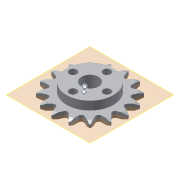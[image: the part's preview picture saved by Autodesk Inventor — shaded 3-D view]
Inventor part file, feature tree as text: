
AUTODESK INVENTOR PART (.ipt)
format: ipt  version: 2013 (Build 170138000, 138)  size: 414,208 bytes
history: native  units: in
note: dims shown in document units (in); Inventor stores cm internally (conversion verified against a paired STEP export)
features: other x17, plane x1
ambient origin geometry x8: Origin, YZ Plane, XZ Plane, XY Plane, X Axis, Y Axis, Z Axis, Center Point
bodies: Solid1 (feature_tree)
feature tree (18):
  other  "Tetrix sprocket 16T.ipt"
  other  "sprocket_25_16t_tetrix::Tetrix sprocket 16T.ipt"
  other  "TaggingFeature1"
  other  "FRONT"
  other  "TOP"
  other  "RIGHT"
  plane  "Work Plane4"
  other  "A_1"
  other  "A_2"
  other  "A_4"
  other  "A_5"
  other  "A_6"
  other  "A_3"
  other  "A_7"
  other  "A_8"
  other  "A_9"
  other  "iComposite:2"
  other  "iComposite:1"
